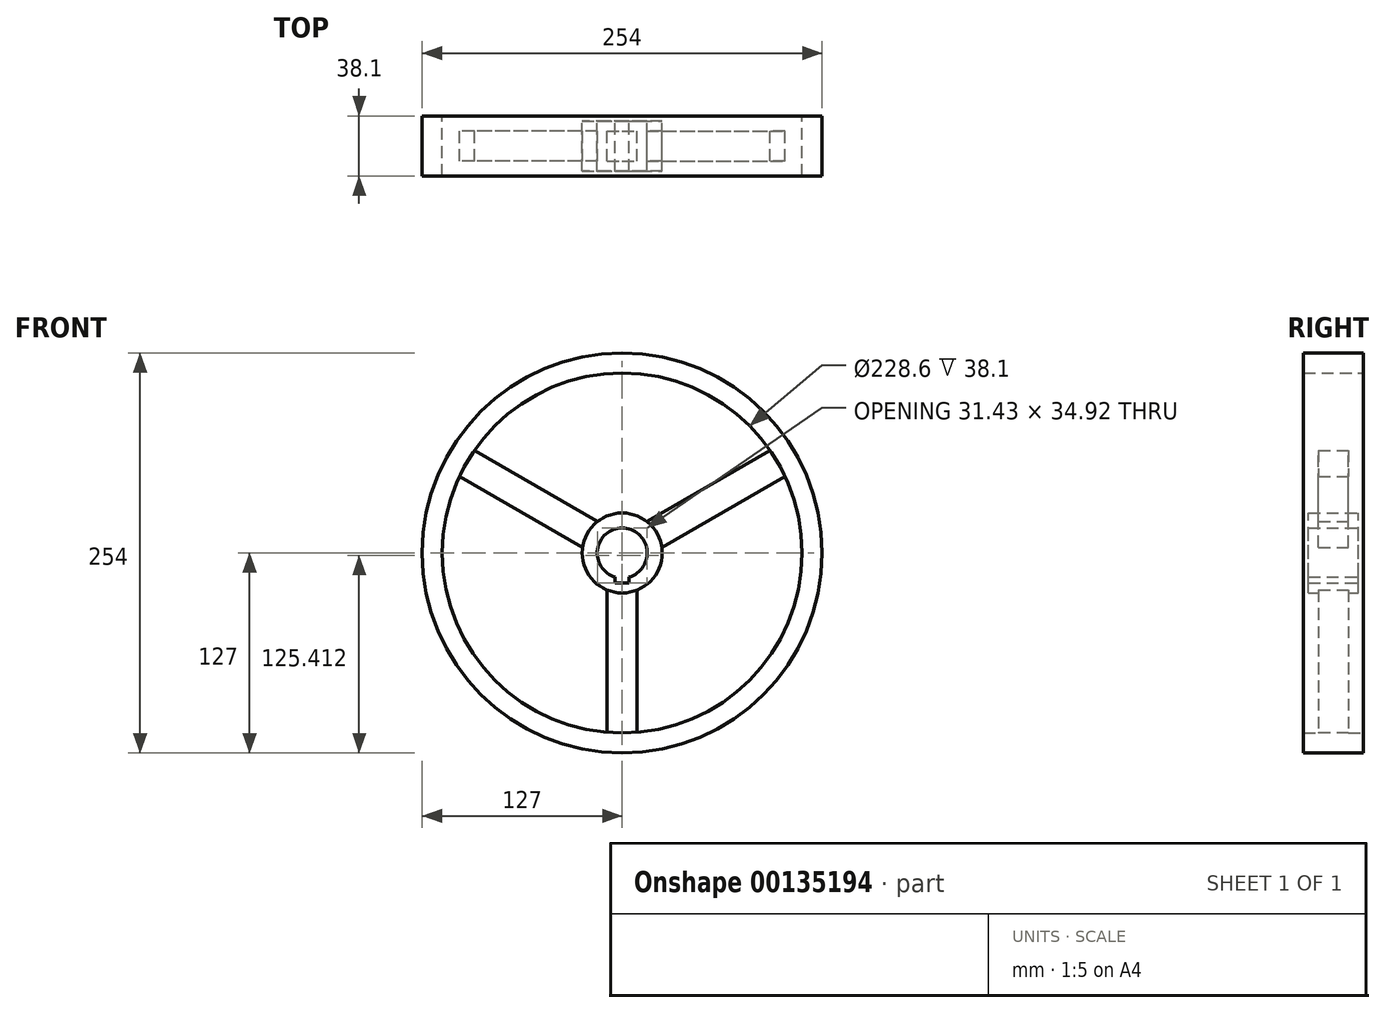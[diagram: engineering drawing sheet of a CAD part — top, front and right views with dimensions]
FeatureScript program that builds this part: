
annotation { "Feature Type Name" : "Feature", "Feature Type Description" : "" }
export const myFeature = defineFeature(function(context is Context, id is Id, definition is map)
    precondition{}
    {
        {
            var Q0;
            Q0=qCreatedBy(makeId("Front.planeOp"),FACE);
            var sketch = newSketch(context, id + "F0", { "sketchPlane" : qUnion([Q0])});
            skArc(sketch, "E0", {"start": v(4.45, -15.24) * mm, "mid": v(0, 15.88) * mm, "end": v(-4.45, -15.24) * mm});
            skCircle(sketch, "E1", {"center": v(0, 0) * mm, "radius": 25.4 * mm});
            skPoint(sketch, "E2", {"position": v(0, -19.05) * mm});
            skLineSegment(sketch, "E3", {"start": v(-4.45, -19.05) * mm, "end": v(4.45, -19.05) * mm});
            skLineSegment(sketch, "E4", {"start": v(-4.45, -19.05) * mm, "end": v(-4.45, -15.24) * mm});
            skLineSegment(sketch, "E5", {"start": v(4.45, -19.05) * mm, "end": v(4.45, -15.24) * mm});
            skCircle(sketch, "E6", {"center": v(0, 0) * mm, "radius": 114.3 * mm});
            skCircle(sketch, "E7", {"center": v(0, 0) * mm, "radius": 127 * mm});
            skLineSegment(sketch, "E8", {"start": v(0, -25.4) * mm, "end": v(0, -114.3) * mm, "construction": true});
            skLineSegment(sketch, "E9.1.0", {"start": v(22, 12.7) * mm, "end": v(98.99, 57.15) * mm, "construction": true});
            skLineSegment(sketch, "E9.2.0", {"start": v(-22, 12.7) * mm, "end": v(-98.99, 57.15) * mm, "construction": true});
            skLineSegment(sketch, "E10", {"start": v(-9.53, -23.55) * mm, "end": v(-9.52, -113.9) * mm});
            skLineSegment(sketch, "E11.MirrorCS", {"start": v(9.53, -23.55) * mm, "end": v(9.52, -113.9) * mm});
            skLineSegment(sketch, "E12.1.0", {"start": v(25.15, 3.52) * mm, "end": v(103.4, 48.7) * mm});
            skLineSegment(sketch, "E12.1.1", {"start": v(15.63, 20.02) * mm, "end": v(93.88, 65.2) * mm});
            skLineSegment(sketch, "E12.2.0", {"start": v(-15.63, 20.02) * mm, "end": v(-93.88, 65.2) * mm});
            skLineSegment(sketch, "E12.2.1", {"start": v(-25.15, 3.52) * mm, "end": v(-103.4, 48.7) * mm});
            skSolve(sketch);
        }
        {
            var Q0;
            Q0 = qSketchRegion(id + "F0", true);
            extrude(context, id + "F1", {"entities" : qUnion([Q0]), "endBound" : BoundingType.SYMMETRIC, "depth" : 38.1 * mm});
        }
        {
            var Q0;
            {var subQ0=sQuery(id+"F0.wireOp",EDGE,"E12.2.0");Q0=makeQuery(id+"F0.imprint","IMPRINT",FACE,{"disambiguationData":[TD([[makeQuery(id+"F0.imprint","IMPRINT",EDGE,{"derivedFrom":subQ0}),1.0]])]});}
            var Q1;
            {var subQ0=sQuery(id+"F0.wireOp",EDGE,"E12.1.0");Q1=makeQuery(id+"F0.imprint","IMPRINT",FACE,{"disambiguationData":[TD([[makeQuery(id+"F0.imprint","IMPRINT",EDGE,{"derivedFrom":subQ0}),1.0]])]});}
            var Q2;
            {var subQ0=sQuery(id+"F0.wireOp",EDGE,"E10");Q2=makeQuery(id+"F0.imprint","IMPRINT",FACE,{"disambiguationData":[TD([[makeQuery(id+"F0.imprint","IMPRINT",EDGE,{"derivedFrom":subQ0}),1.0]])]});}
            extrude(context, id + "F2", {"entities" : qUnion([Q0, Q1, Q2]), "operationType" : NewBodyOperationType.ADD, "endBound" : BoundingType.SYMMETRIC, "depth" : 19.05 * mm});
        }
        {
            var Q0;
            Q0=makeQuery(id+"F0.imprint","IMPRINT",FACE,{"disambiguationData":[TD([[makeQuery(id+"F0.imprint","IMPRINT",EDGE,{"derivedFrom":sQuery(id+"F0.wireOp",EDGE,"E0")}),-1.0]])]});
            extrude(context, id + "F3", {"entities" : qUnion([Q0]), "operationType" : NewBodyOperationType.ADD, "endBound" : BoundingType.SYMMETRIC, "depth" : 31.75 * mm});
        }
    });
